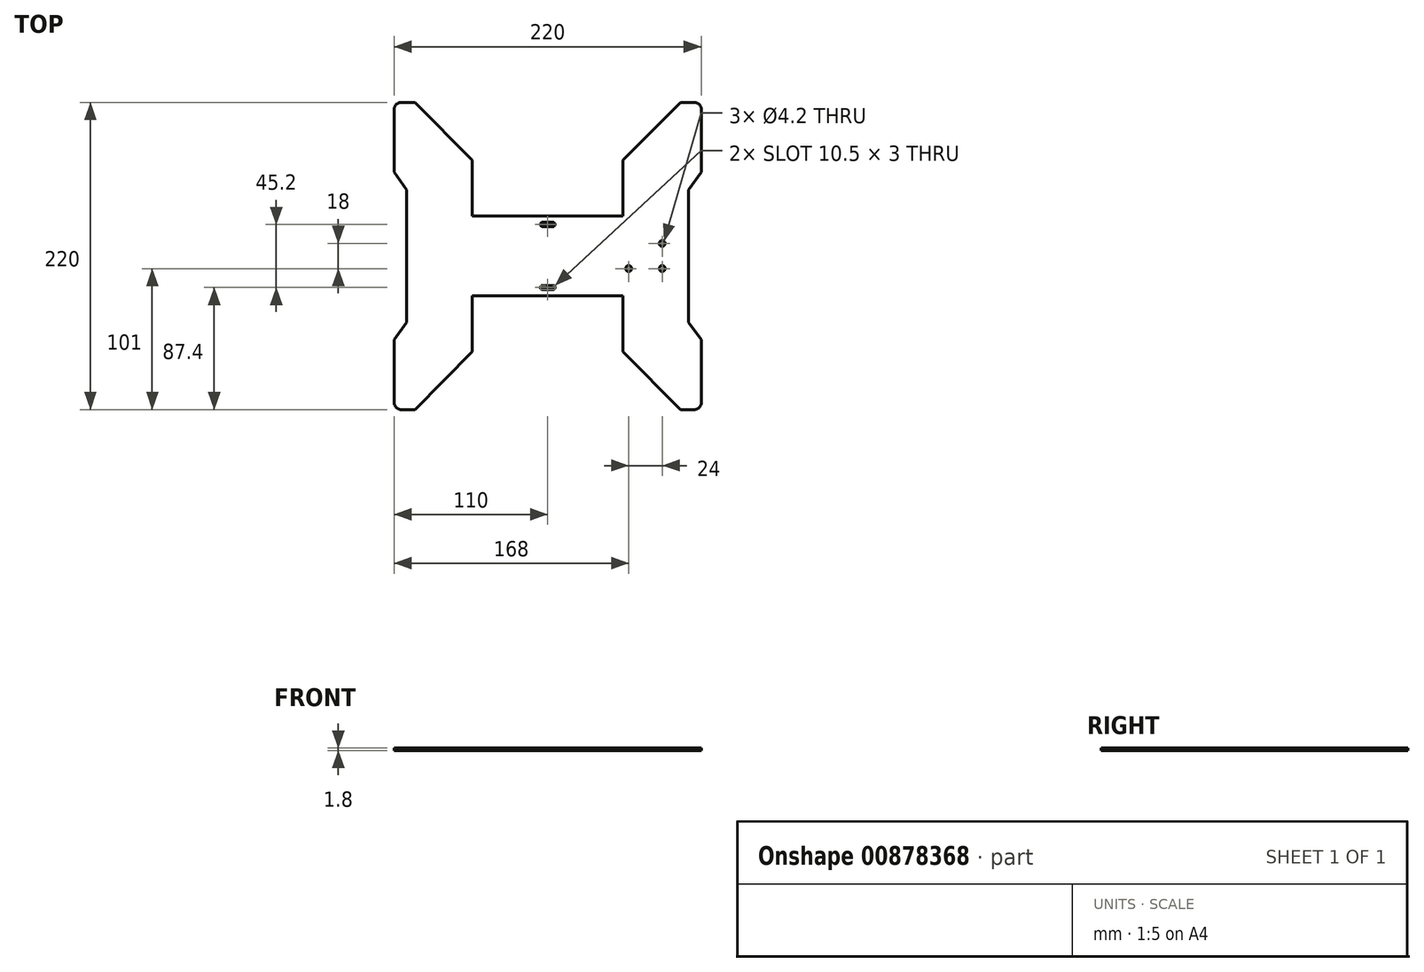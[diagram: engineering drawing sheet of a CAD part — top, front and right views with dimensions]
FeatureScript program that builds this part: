
annotation { "Feature Type Name" : "Feature", "Feature Type Description" : "" }
export const myFeature = defineFeature(function(context is Context, id is Id, definition is map)
    precondition{}
    {
        {
            var Q0;
            Q0=qCreatedBy(makeId("Top.planeOp"),FACE);
            var sketch = newSketch(context, id + "F0", { "sketchPlane" : qUnion([Q0])});
            skLineSegment(sketch, "E0.bottom", {"start": v(54, 28.5) * mm, "end": v(-54, 28.5) * mm});
            skLineSegment(sketch, "E0.top", {"start": v(54, -28.5) * mm, "end": v(-54, -28.5) * mm});
            skPoint(sketch, "E0.middle", {"position": v(0, 0) * mm});
            skLineSegment(sketch, "E1.top", {"start": v(-105, 110) * mm, "end": v(-95, 110) * mm});
            skLineSegment(sketch, "E1.left", {"start": v(-110, 60) * mm, "end": v(-110, 105) * mm});
            skLineSegment(sketch, "E1.right", {"start": v(-54, 28.5) * mm, "end": v(-54, 68.5) * mm});
            skLineSegment(sketch, "E2.top", {"start": v(-105, -110) * mm, "end": v(-95, -110) * mm});
            skLineSegment(sketch, "E2.left", {"start": v(-110, 105) * mm, "end": v(-110, 60) * mm});
            skLineSegment(sketch, "E2.right", {"start": v(110, 105) * mm, "end": v(110, 60) * mm});
            skLineSegment(sketch, "E3.left", {"start": v(-110, -60) * mm, "end": v(-110, -105) * mm});
            skLineSegment(sketch, "E3.right", {"start": v(-54, -28.5) * mm, "end": v(-54, -68.5) * mm});
            skLineSegment(sketch, "E4.top", {"start": v(105, 110) * mm, "end": v(95, 110) * mm});
            skLineSegment(sketch, "E4.left", {"start": v(110, 60) * mm, "end": v(110, 105) * mm});
            skLineSegment(sketch, "E4.right", {"start": v(54, 28.5) * mm, "end": v(54, 68.5) * mm});
            skLineSegment(sketch, "E5.top", {"start": v(95, -110) * mm, "end": v(105, -110) * mm});
            skLineSegment(sketch, "E5.left", {"start": v(54, -28.5) * mm, "end": v(54, -68.5) * mm});
            skLineSegment(sketch, "E5.right", {"start": v(110, -60) * mm, "end": v(110, -105) * mm});
            skPoint(sketch, "E6.visualSharp", {"position": v(-110, 110) * mm});
            skArc(sketch, "E6.filletArc", {"start": v(-105, 110) * mm, "mid": v(-108.54, 108.54) * mm, "end": v(-110, 105) * mm});
            skPoint(sketch, "E7.visualSharp", {"position": v(110, 110) * mm});
            skArc(sketch, "E7.filletArc", {"start": v(110, 105) * mm, "mid": v(108.54, 108.54) * mm, "end": v(105, 110) * mm});
            skPoint(sketch, "E8.visualSharp", {"position": v(110, -110) * mm});
            skArc(sketch, "E8.filletArc", {"start": v(105, -110) * mm, "mid": v(108.54, -108.54) * mm, "end": v(110, -105) * mm});
            skPoint(sketch, "E9.visualSharp", {"position": v(-110, -110) * mm});
            skArc(sketch, "E9.filletArc", {"start": v(-110, -105) * mm, "mid": v(-108.54, -108.54) * mm, "end": v(-105, -110) * mm});
            skLineSegment(sketch, "E10", {"start": v(-101, 47.5) * mm, "end": v(-101, -47.5) * mm});
            skLineSegment(sketch, "E11", {"start": v(101, 47.5) * mm, "end": v(101, -47.5) * mm});
            skLineSegment(sketch, "E12", {"start": v(-95, 110) * mm, "end": v(-54, 68.5) * mm});
            skLineSegment(sketch, "E13", {"start": v(-110, 60) * mm, "end": v(-101, 47.5) * mm});
            skPoint(sketch, "E0.right.start.orphan", {"position": v(-110, 28.5) * mm});
            skLineSegment(sketch, "E14", {"start": v(0, 0) * mm, "end": v(-129.86, 0) * mm, "construction": true});
            skPoint(sketch, "E14.endSnap0", {"position": v(-101, 0) * mm});
            skLineSegment(sketch, "E15.MirrorCS", {"start": v(-95, -110) * mm, "end": v(-54, -68.5) * mm});
            skLineSegment(sketch, "E16.MirrorCS", {"start": v(-110, -60) * mm, "end": v(-101, -47.5) * mm});
            skLineSegment(sketch, "E17.MirrorCS", {"start": v(-101, -47.5) * mm, "end": v(-101, 47.5) * mm});
            skLineSegment(sketch, "E18", {"start": v(0, 0) * mm, "end": v(0, 157.04) * mm, "construction": true});
            skLineSegment(sketch, "E19.MirrorCS", {"start": v(95, 110) * mm, "end": v(54, 68.5) * mm});
            skLineSegment(sketch, "E20.MirrorCS", {"start": v(110, 60) * mm, "end": v(101, 47.5) * mm});
            skLineSegment(sketch, "E21.MirrorCS", {"start": v(95, -110) * mm, "end": v(54, -68.5) * mm});
            skLineSegment(sketch, "E22.MirrorCS", {"start": v(110, -60) * mm, "end": v(101, -47.5) * mm});
            skLineSegment(sketch, "E23.trimOffspring", {"start": v(95, 110) * mm, "end": v(105, 110) * mm});
            skPoint(sketch, "E24.orphan", {"position": v(-110, -28.5) * mm});
            skPoint(sketch, "E25.orphan", {"position": v(-54, -110) * mm});
            skPoint(sketch, "E0.left.start.orphan", {"position": v(110, 28.5) * mm});
            skPoint(sketch, "E26.orphan", {"position": v(110, -28.5) * mm});
            skLineSegment(sketch, "E27", {"start": v(70, -59.24) * mm, "end": v(70, 58.14) * mm, "construction": true});
            skLineSegment(sketch, "E28", {"start": v(0, 0) * mm, "end": v(94.3, 0) * mm, "construction": true});
            skLineSegment(sketch, "E29.bottom", {"start": v(82, -9) * mm, "end": v(58, -9) * mm, "construction": true});
            skLineSegment(sketch, "E29.top", {"start": v(82, 9) * mm, "end": v(58, 9) * mm, "construction": true});
            skLineSegment(sketch, "E29.left", {"start": v(82, -9) * mm, "end": v(82, 9) * mm, "construction": true});
            skLineSegment(sketch, "E29.right", {"start": v(58, -9) * mm, "end": v(58, 9) * mm, "construction": true});
            skPoint(sketch, "E29.middle", {"position": v(70, 0) * mm});
            skCircle(sketch, "E30", {"center": v(82, -9) * mm, "radius": 2.1 * mm});
            skCircle(sketch, "E31", {"center": v(58, -9) * mm, "radius": 2.1 * mm});
            skCircle(sketch, "E32", {"center": v(82, 9) * mm, "radius": 2.1 * mm});
            skLineSegment(sketch, "E33", {"start": v(0, 28.5) * mm, "end": v(0, 24.1) * mm, "construction": true});
            skLineSegment(sketch, "E34", {"start": v(0, 24.1) * mm, "end": v(-3.75, 24.1) * mm, "construction": true});
            skLineSegment(sketch, "E35", {"start": v(-3.75, 21.1) * mm, "end": v(3.75, 21.1) * mm, "construction": true});
            skLineSegment(sketch, "E36", {"start": v(5.25, 22.6) * mm, "end": v(5.25, 23.15) * mm, "construction": true});
            skLineSegment(sketch, "E37", {"start": v(3.75, 24.1) * mm, "end": v(0, 24.1) * mm, "construction": true});
            skLineSegment(sketch, "E38.bottom", {"start": v(3.75, 24.1) * mm, "end": v(-3.75, 24.1) * mm});
            skLineSegment(sketch, "E38.top", {"start": v(3.75, 21.1) * mm, "end": v(-3.75, 21.1) * mm});
            skLineSegment(sketch, "E39.MirrorCS", {"start": v(-3.75, -21.1) * mm, "end": v(3.75, -21.1) * mm, "construction": true});
            skLineSegment(sketch, "E40.MirrorCS", {"start": v(0, -24.1) * mm, "end": v(-3.75, -24.1) * mm, "construction": true});
            skLineSegment(sketch, "E41.bottom", {"start": v(3.75, -21.1) * mm, "end": v(-3.75, -21.1) * mm});
            skLineSegment(sketch, "E41.top", {"start": v(3.75, -24.1) * mm, "end": v(-3.75, -24.1) * mm});
            skPoint(sketch, "E42.centerSnap0", {"position": v(5.25, 22.6) * mm});
            skPoint(sketch, "E43.first.point", {"position": v(5.25, 23.15) * mm});
            skPoint(sketch, "E43.second.point", {"position": v(3.75, 24.1) * mm});
            skPoint(sketch, "E43.third.point", {"position": v(4.24, 21.1) * mm});
            skArc(sketch, "E44", {"start": v(3.75, 21.1) * mm, "mid": v(5.25, 22.6) * mm, "end": v(3.75, 24.1) * mm});
            skPoint(sketch, "E44.third.point", {"position": v(3.75, 21.1) * mm});
            skPoint(sketch, "E45.orphan", {"position": v(5.25, 24.1) * mm});
            skPoint(sketch, "E46.orphan", {"position": v(5.25, 21.1) * mm});
            skArc(sketch, "E47", {"start": v(-3.75, 24.1) * mm, "mid": v(-5.25, 22.6) * mm, "end": v(-3.75, 21.1) * mm});
            skPoint(sketch, "E47.first.point", {"position": v(-5.25, 22.6) * mm});
            skPoint(sketch, "E47.second.point", {"position": v(-3.75, 24.1) * mm});
            skPoint(sketch, "E47.third.point", {"position": v(-3.75, 21.1) * mm});
            skPoint(sketch, "E48.orphan", {"position": v(-5.25, 24.1) * mm});
            skPoint(sketch, "E49.orphan", {"position": v(-5.25, 21.1) * mm});
            skArc(sketch, "E50.MirrorCS", {"start": v(3.75, -21.1) * mm, "mid": v(5.25, -22.6) * mm, "end": v(3.75, -24.1) * mm});
            skArc(sketch, "E51.MirrorCS", {"start": v(-3.75, -24.1) * mm, "mid": v(-5.25, -22.6) * mm, "end": v(-3.75, -21.1) * mm});
            skPoint(sketch, "E52.orphan", {"position": v(5.25, -21.1) * mm});
            skPoint(sketch, "E53.MirrorCS.end.orphan", {"position": v(5.25, -24.1) * mm});
            skPoint(sketch, "E54.MirrorCS.end.orphan", {"position": v(0, -24.1) * mm});
            skPoint(sketch, "E55.orphan", {"position": v(-5.25, -24.1) * mm});
            skPoint(sketch, "E56.MirrorCS.end.orphan", {"position": v(-5.25, -21.1) * mm});
            skSolve(sketch);
        }
        {
            var Q0;
            Q0=makeQuery(id+"F0.imprint","IMPRINT",FACE,{"disambiguationData":[TD([[makeQuery(id+"F0.imprint","IMPRINT",EDGE,{"derivedFrom":sQuery(id+"F0.wireOp",EDGE,"E0.bottom")}),1.0]])]});
            extrude(context, id + "F1", {"entities" : qUnion([Q0]), "depth" : 1.8 * mm, "offsetDistance" : 25 * mm});
        }
    });
